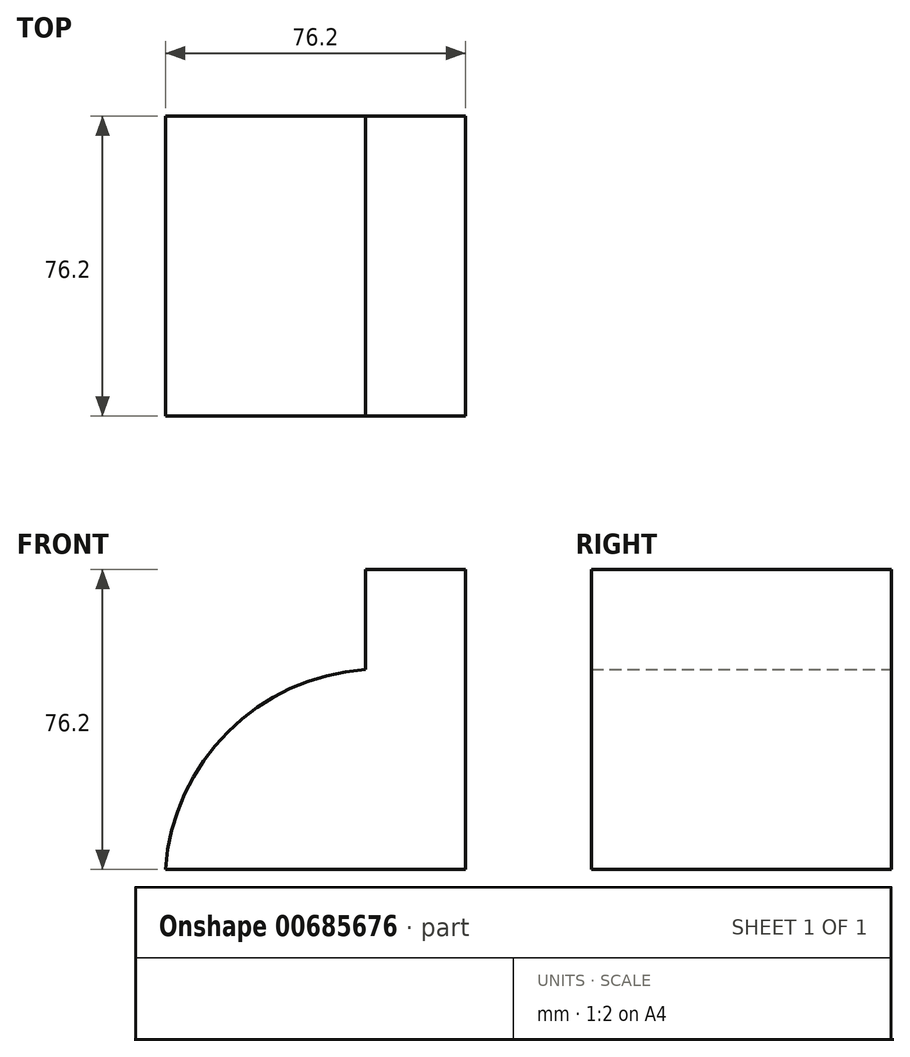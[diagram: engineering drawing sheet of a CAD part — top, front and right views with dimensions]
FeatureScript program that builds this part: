
annotation { "Feature Type Name" : "Feature", "Feature Type Description" : "" }
export const myFeature = defineFeature(function(context is Context, id is Id, definition is map)
    precondition{}
    {
        {
            var Q0;
            Q0=qCreatedBy(makeId("Front.planeOp"),FACE);
            var sketch = newSketch(context, id + "F0", { "sketchPlane" : qUnion([Q0])});
            skLineSegment(sketch, "E0", {"start": v(0, 0) * mm, "end": v(0, 25.4) * mm});
            skLineSegment(sketch, "E1", {"start": v(0, 25.4) * mm, "end": v(25.4, 25.4) * mm});
            skLineSegment(sketch, "E2", {"start": v(25.4, 25.4) * mm, "end": v(25.4, -50.8) * mm});
            skLineSegment(sketch, "E3", {"start": v(25.4, -50.8) * mm, "end": v(-50.8, -50.8) * mm});
            skArc(sketch, "E4", {"start": v(0, 0) * mm, "mid": v(-34.94, -15.86) * mm, "end": v(-50.8, -50.8) * mm});
            skSolve(sketch);
        }
        {
            var Q0;
            Q0 = qSketchRegion(id + "F0", true);
            extrude(context, id + "F1", {"entities" : qUnion([Q0]), "depth" : 76.2 * mm, "offsetDistance" : 25.4 * mm});
        }
    });
